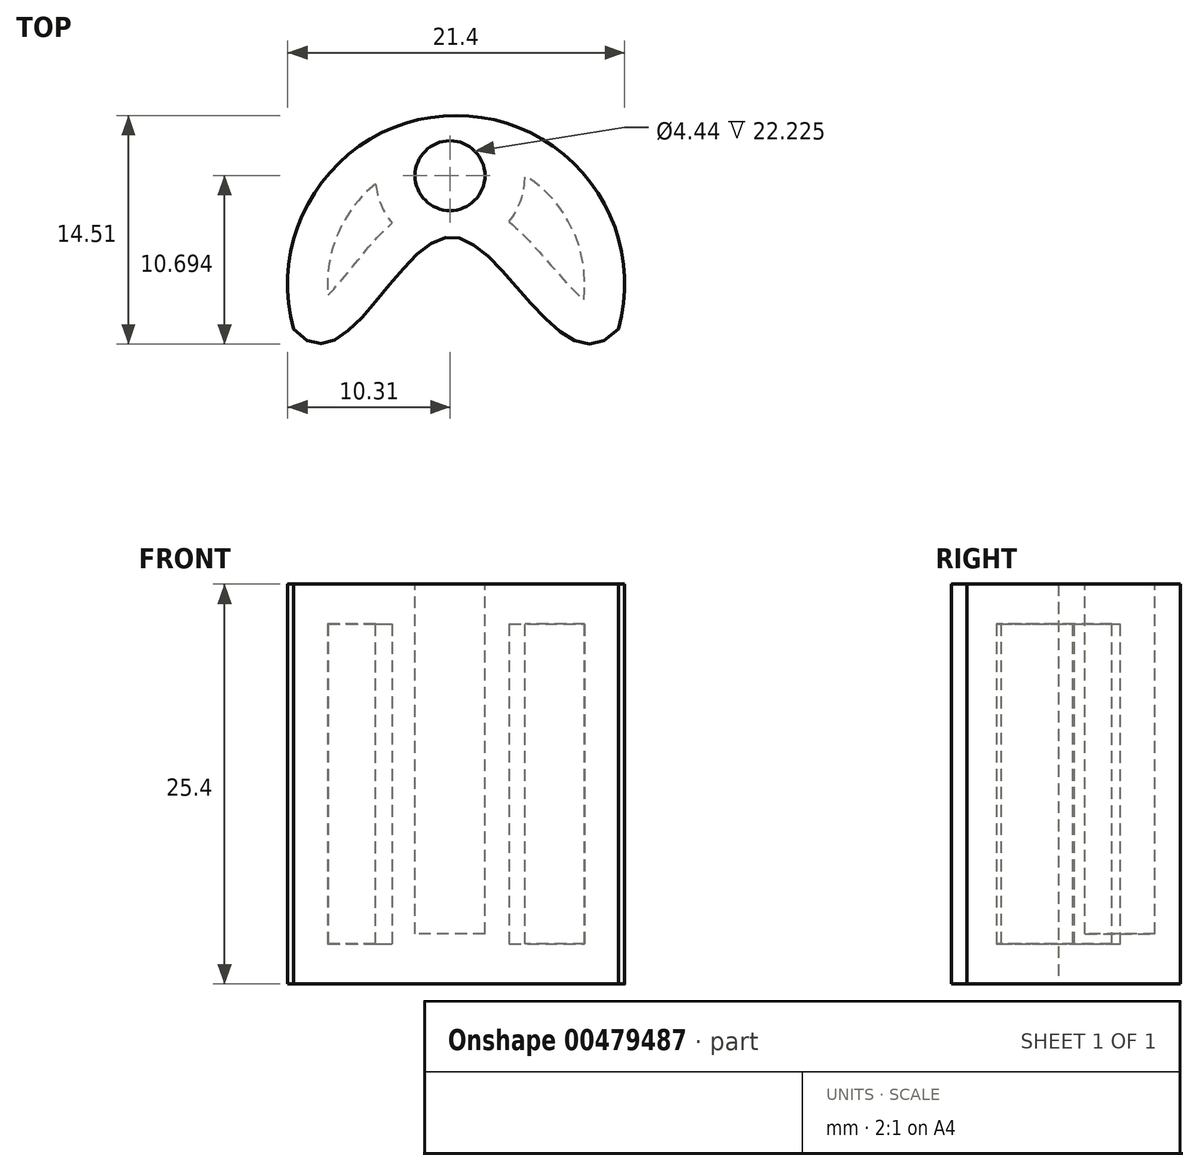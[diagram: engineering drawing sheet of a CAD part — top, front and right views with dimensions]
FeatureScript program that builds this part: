
annotation { "Feature Type Name" : "Feature", "Feature Type Description" : "" }
export const myFeature = defineFeature(function(context is Context, id is Id, definition is map)
    precondition{}
    {
        {
            var Q0;
            Q0=qCreatedBy(makeId("Top.planeOp"),FACE);
            var sketch = newSketch(context, id + "F0", { "sketchPlane" : qUnion([Q0])});
            skArc(sketch, "E0", {"start": v(10.7, 0) * mm, "mid": v(0.39, 13.55) * mm, "end": v(-9.93, 0) * mm});
            skFitSpline(sketch, "E1", {"points": [v(-9.93, 0) * mm, v(0, 5.83) * mm, v(10.7, 0) * mm], "startDerivative": vector(19.83, -24.04) * mm, "endDerivative": vector(21.43, 23.85) * mm});
            skSolve(sketch);
        }
        {
            var Q0;
            Q0=makeQuery(id+"F0.imprint","IMPRINT",FACE,{"disambiguationData":[TD([[makeQuery(id+"F0.imprint","IMPRINT",EDGE,{"derivedFrom":sQuery(id+"F0.wireOp",EDGE,"E0")}),1.0]])]});
            extrude(context, id + "F1", {"entities" : qUnion([Q0]), "depth" : 25.4 * mm});
        }
        {
            var Q0;
            Q0=makeQuery(id+"F1.opExtrude","CAP_FACE",FACE,{"disambiguationData":[OSD([sQuery(id+"F0.wireOp",EDGE,"E0"),sQuery(id+"F0.wireOp",EDGE,"E1")])],"isStart":false});
            var sketch = newSketch(context, id + "F2", { "sketchPlane" : qUnion([Q0])});
            skCircle(sketch, "E2", {"center": v(0, 9.73) * mm, "radius": 2.22 * mm});
            skSolve(sketch);
        }
        {
            var Q0;
            Q0=makeQuery(id+"F2.imprint","IMPRINT",FACE,{"disambiguationData":[TD([[makeQuery(id+"F2.imprint","IMPRINT",EDGE,{"derivedFrom":sQuery(id+"F2.wireOp",EDGE,"E2")}),1.0]])]});
            var Q1;
            Q1=sQuery(id+"F2.wireOp",EDGE,"E2");
            extrude(context, id + "F3", {"entities" : qUnion([Q0]), "operationType" : NewBodyOperationType.REMOVE, "surfaceEntities" : qUnion([Q1]), "oppositeDirection" : true, "depth" : 22.22 * mm});
        }
        {
            var Q0;
            Q0=makeQuery(id+"F1.opExtrude","SWEPT_FACE",FACE,{"disambiguationData":[OSD([sQuery(id+"F0.wireOp",EDGE,"E0")])]});
            var Q1;
            Q1=makeQuery(id+"F1.opExtrude","SWEPT_BODY",BODY,{"disambiguationData":[OSD([sQuery(id+"F0.wireOp",EDGE,"E0"),sQuery(id+"F0.wireOp",EDGE,"E1")])]});
            shell(context, id + "F4", {"isHollow" : true, "entities" : qUnion([Q0]), "parts" : qUnion([Q1]), "thickness" : 2.54 * mm});
        }
    });
